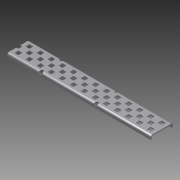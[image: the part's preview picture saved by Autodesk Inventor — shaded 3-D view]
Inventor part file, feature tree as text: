
AUTODESK INVENTOR PART (.ipt)
format: ipt  version: 2014 SP1 (Build 180222100, 222)  size: 889,856 bytes
history: native  units: in
note: dims shown in document units (in); Inventor stores cm internally (conversion verified against a paired STEP export)
features: extrude x2, sketch x2, other x1, imported_body x1
ambient origin geometry x8: Origin, YZ Plane, XZ Plane, XY Plane, X Axis, Y Axis, Z Axis, Center Point
bodies: Body1 (feature_tree)
feature tree (6):
  parser-record x1  (decoder bookkeeping rows leaked as tree rows — omitted from the tree; the rows remain in map.json)
  imported_body  "Base1"
  extrude  "Extrusion1"  Depth=1.0in TaperAngle=0.0deg
  extrude  "Extrusion2"  Depth=0.125in
  sketch  "Sketch1"  dims[d0=1.0in d1=1.0in d2=0.0in]
  sketch  "Sketch2"  dims[d3=10.0in d4=0.0in d5=0.125in]
